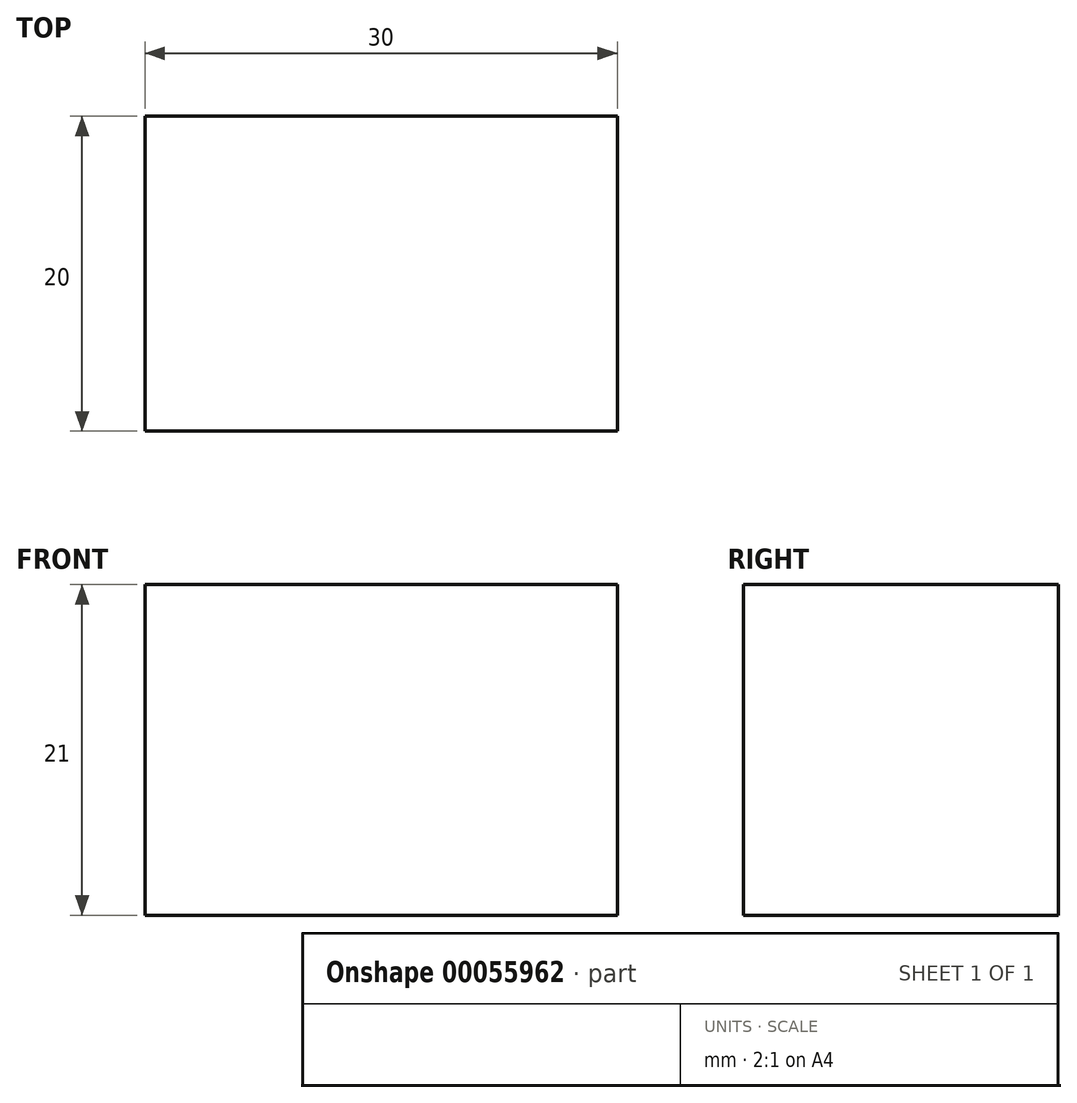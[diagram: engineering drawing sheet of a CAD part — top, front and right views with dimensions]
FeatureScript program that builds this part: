
annotation { "Feature Type Name" : "Feature", "Feature Type Description" : "" }
export const myFeature = defineFeature(function(context is Context, id is Id, definition is map)
    precondition{}
    {
        {
            var Q0;
            Q0=qCreatedBy(makeId("Right.planeOp"),FACE);
            var sketch = newSketch(context, id + "F0", { "sketchPlane" : qUnion([Q0])});
            skLineSegment(sketch, "E0", {"start": v(0, 5) * mm, "end": v(20, 5) * mm, "construction": true});
            skLineSegment(sketch, "E1", {"start": v(0, 5) * mm, "end": v(-19.93, 5) * mm, "construction": true});
            skLineSegment(sketch, "E2.top", {"start": v(0, 5) * mm, "end": v(10, 5) * mm});
            skLineSegment(sketch, "E2.left", {"start": v(0, 0) * mm, "end": v(0, 5) * mm});
            skLineSegment(sketch, "E3.top", {"start": v(-10, -15) * mm, "end": v(10, -15) * mm});
            skLineSegment(sketch, "E3.left", {"start": v(-10, 5) * mm, "end": v(-10, -15) * mm});
            skLineSegment(sketch, "E3.right", {"start": v(10, 5) * mm, "end": v(10, -15) * mm});
            skLineSegment(sketch, "E4", {"start": v(0, 5) * mm, "end": v(-10, 5) * mm});
            skSolve(sketch);
        }
        {
            var Q0;
            {var subQ0=sQuery(id+"F0.wireOp",EDGE,"E2.top");Q0=makeQuery(id+"F0.imprint","IMPRINT",FACE,{"disambiguationData":[TD([[makeQuery(id+"F0.imprint","IMPRINT",EDGE,{"derivedFrom":subQ0}),-1.0]])]});}
            var Q1;
            Q1=makeQuery(id+"F0.imprint","IMPRINT",FACE,{"disambiguationData":[TD([[makeQuery(id+"F0.imprint","IMPRINT",EDGE,{"derivedFrom":sQuery(id+"F0.wireOp",EDGE,"7b671ddb-c26b-43ad-9a77-c9769348d744")}),-1.0]])]});
            var Q2;
            {var subQ0=sQuery(id+"F0.wireOp",EDGE,"aeaad599-9b53-4a81-9b34-b4e3524915ed.top");Q2=makeQuery(id+"F0.imprint","IMPRINT",FACE,{"disambiguationData":[TD([[makeQuery(id+"F0.imprint","IMPRINT",EDGE,{"derivedFrom":subQ0}),1.0]])]});}
            extrude(context, id + "F1", {"entities" : qUnion([Q0, Q1, Q2]), "depth" : 30 * mm});
        }
        {
            var Q0;
            Q0=makeQuery(id+"F1.opExtrude","SWEPT_FACE",FACE,{"disambiguationData":[OSD([sQuery(id+"F0.wireOp",EDGE,"E2.top"),sQuery(id+"F0.wireOp",EDGE,"aeaad599-9b53-4a81-9b34-b4e3524915ed.top")])]});
            extrude(context, id + "F2", {"entities" : qUnion([Q0]), "operationType" : NewBodyOperationType.ADD, "depth" : 1 * mm});
        }
    });
